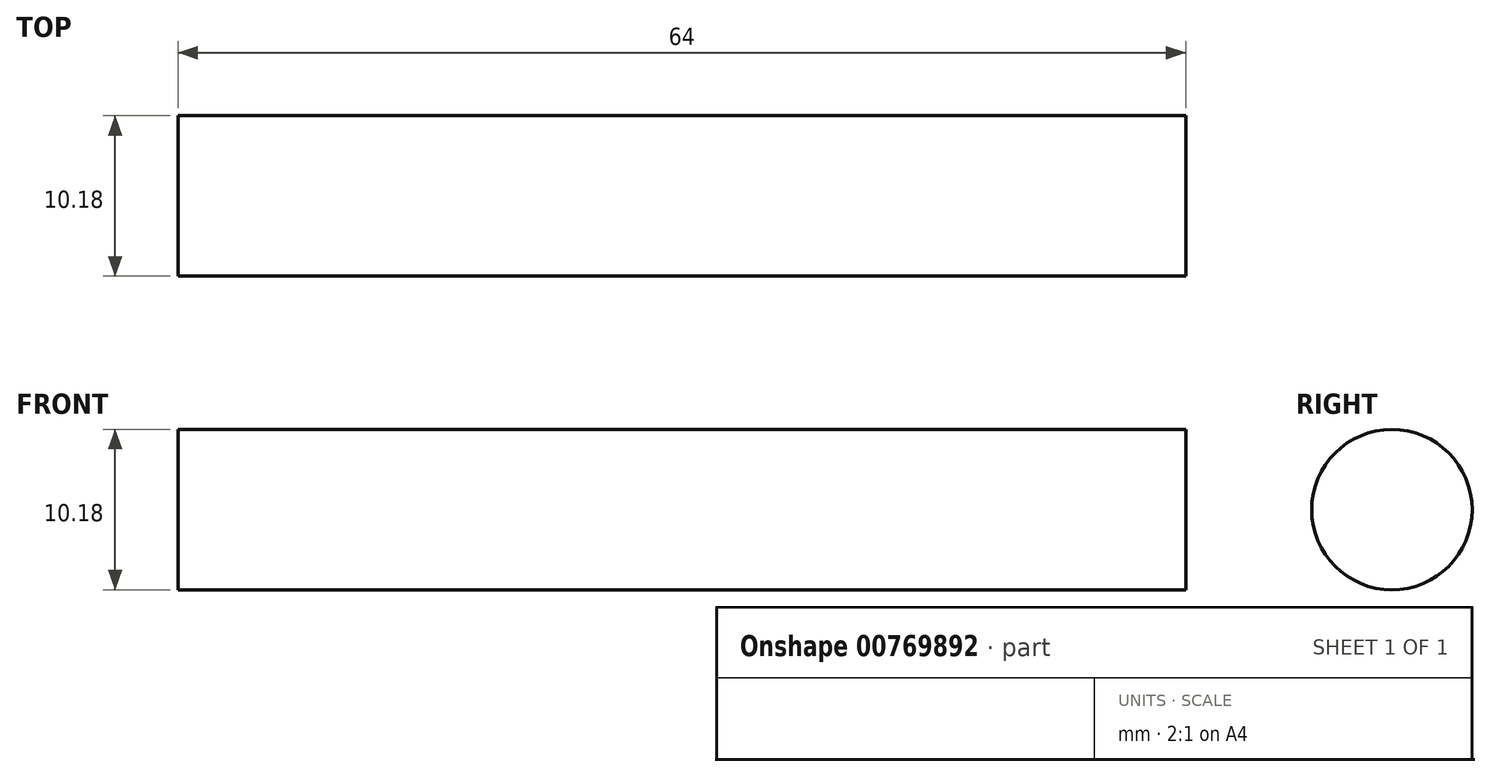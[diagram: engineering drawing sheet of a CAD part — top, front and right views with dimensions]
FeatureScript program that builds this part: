
annotation { "Feature Type Name" : "Feature", "Feature Type Description" : "" }
export const myFeature = defineFeature(function(context is Context, id is Id, definition is map)
    precondition{}
    {
        {
            var Q0;
            Q0=qCreatedBy(makeId("Right.planeOp"),FACE);
            var sketch = newSketch(context, id + "F0", { "sketchPlane" : qUnion([Q0])});
            skCircle(sketch, "E0", {"center": v(0, 0) * mm, "radius": 5.1 * mm});
            skSolve(sketch);
        }
        {
            var Q0;
            Q0 = qSketchRegion(id + "F0", true);
            extrude(context, id + "F1", {"entities" : qUnion([Q0]), "endBound" : BoundingType.SYMMETRIC, "depth" : 64 * mm, "offsetDistance" : 25.4 * mm});
        }
    });
